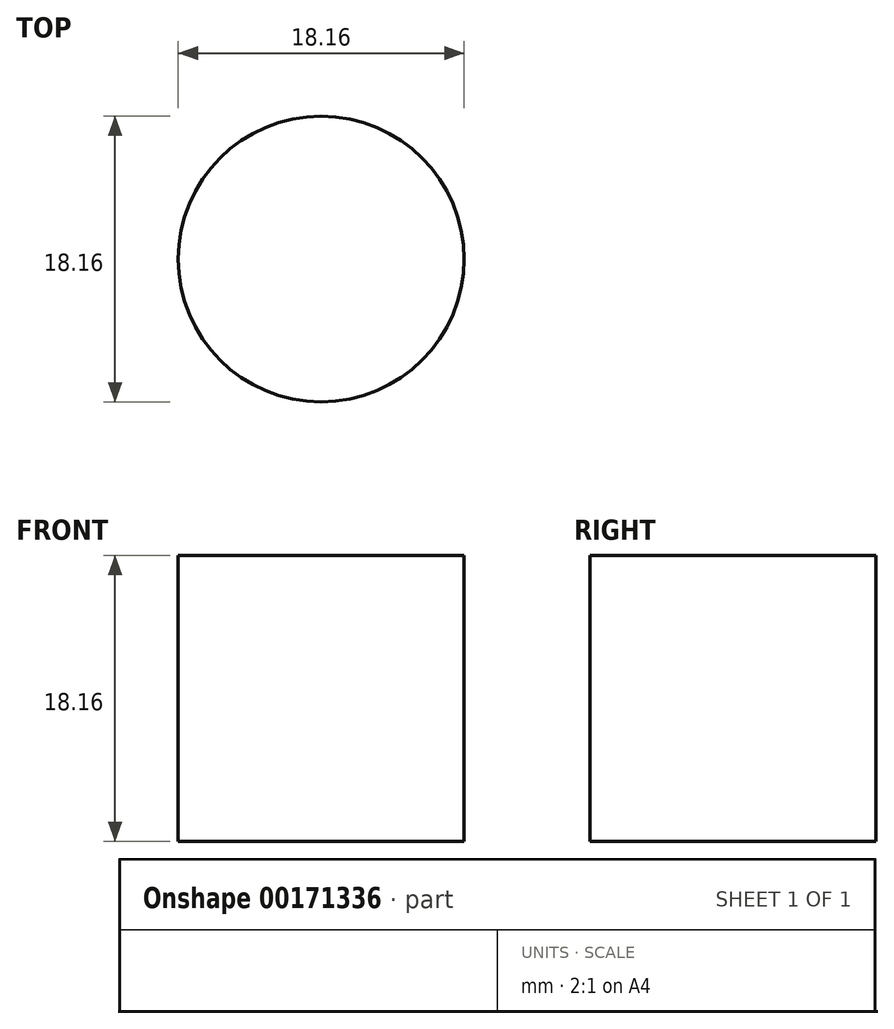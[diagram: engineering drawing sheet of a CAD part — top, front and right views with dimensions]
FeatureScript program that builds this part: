
annotation { "Feature Type Name" : "Feature", "Feature Type Description" : "" }
export const myFeature = defineFeature(function(context is Context, id is Id, definition is map)
    precondition{}
    {
        {
            var Q0;
            Q0=qCreatedBy(makeId("Top.planeOp"),FACE);
            var sketch = newSketch(context, id + "F0", { "sketchPlane" : qUnion([Q0])});
            skCircle(sketch, "E0", {"center": v(0, 0) * mm, "radius": 9.08 * mm});
            skSolve(sketch);
        }
        {
            var Q0;
            Q0 = qSketchRegion(id + "F0", true);
            extrude(context, id + "F1", {"entities" : qUnion([Q0]), "endBound" : BoundingType.SYMMETRIC, "depth" : 18.15 * mm});
        }
    });
